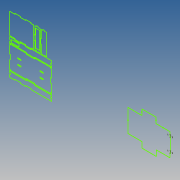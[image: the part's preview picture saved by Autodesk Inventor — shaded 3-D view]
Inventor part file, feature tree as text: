
AUTODESK INVENTOR PART (.ipt)
format: ipt  version: 2020 (Build 240168000, 168)  size: 141,824 bytes
history: native  units: mm
features: sketch x1
ambient origin geometry x8: Origin, YZ Plane, XZ Plane, XY Plane, X Axis, Y Axis, Z Axis, Center Point
feature tree (1):
  sketch  "Sketch1"  dims[d268=3.0mm d269=3.0mm]
